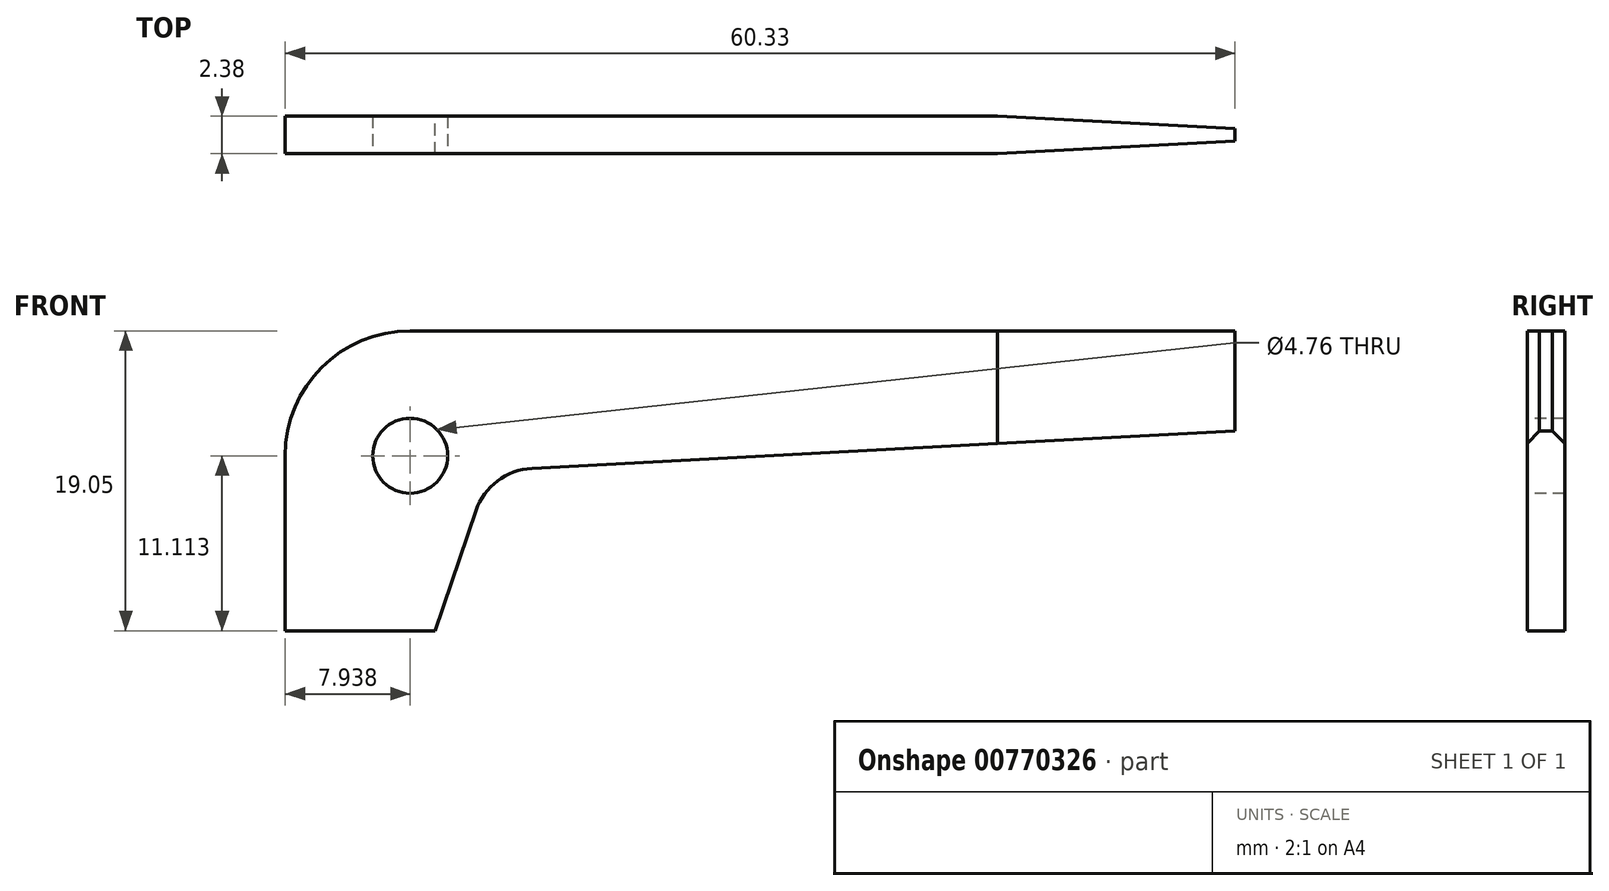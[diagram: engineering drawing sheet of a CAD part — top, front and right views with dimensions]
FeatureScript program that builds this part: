
annotation { "Feature Type Name" : "Feature", "Feature Type Description" : "" }
export const myFeature = defineFeature(function(context is Context, id is Id, definition is map)
    precondition{}
    {
        {
            var Q0;
            Q0=qCreatedBy(makeId("Front.planeOp"),FACE);
            var sketch = newSketch(context, id + "F0", { "sketchPlane" : qUnion([Q0])});
            skLineSegment(sketch, "E0.top", {"start": v(7.94, 19.05) * mm, "end": v(60.33, 19.05) * mm});
            skLineSegment(sketch, "E0.left", {"start": v(0, 0) * mm, "end": v(0, 11.11) * mm});
            skLineSegment(sketch, "E1", {"start": v(9.52, 0) * mm, "end": v(12.12, 7.63) * mm});
            skLineSegment(sketch, "E2", {"start": v(60.33, 12.7) * mm, "end": v(15.66, 10.31) * mm});
            skLineSegment(sketch, "E3", {"start": v(0, 0) * mm, "end": v(9.53, 0) * mm});
            skLineSegment(sketch, "E4", {"start": v(60.33, 19.05) * mm, "end": v(60.33, 12.7) * mm});
            skArc(sketch, "E5", {"start": v(15.66, 10.31) * mm, "mid": v(13.48, 9.51) * mm, "end": v(12.12, 7.63) * mm});
            skPoint(sketch, "E6.visualSharp", {"position": v(0, 19.05) * mm});
            skArc(sketch, "E6.filletArc", {"start": v(7.94, 19.05) * mm, "mid": v(2.32, 16.73) * mm, "end": v(0, 11.11) * mm});
            skSolve(sketch);
        }
        {
            var Q0;
            Q0 = qSketchRegion(id + "F0", true);
            extrude(context, id + "F1", {"entities" : qUnion([Q0]), "depth" : 2.38 * mm, "offsetDistance" : 25.4 * mm});
        }
        {
            var Q0;
            Q0=makeQuery(id+"F1.opExtrude","CAP_FACE",FACE,{"disambiguationData":[OSD([sQuery(id+"F0.wireOp",EDGE,"E0.top"),sQuery(id+"F0.wireOp",EDGE,"E0.left"),sQuery(id+"F0.wireOp",EDGE,"E1"),sQuery(id+"F0.wireOp",EDGE,"E2"),sQuery(id+"F0.wireOp",EDGE,"E3"),sQuery(id+"F0.wireOp",EDGE,"E4"),sQuery(id+"F0.wireOp",EDGE,"E5"),sQuery(id+"F0.wireOp",EDGE,"E6.filletArc")])],"isStart":false});
            var sketch = newSketch(context, id + "F2", { "sketchPlane" : qUnion([Q0])});
            skCircle(sketch, "E7", {"center": v(7.94, 11.11) * mm, "radius": 2.38 * mm});
            skSolve(sketch);
        }
        {
            var Q0;
            Q0=makeQuery(id+"F2.imprint","IMPRINT",FACE,{"disambiguationData":[TD([[makeQuery(id+"F2.imprint","IMPRINT",EDGE,{"derivedFrom":sQuery(id+"F2.wireOp",EDGE,"E7")}),1.0]])]});
            extrude(context, id + "F3", {"entities" : qUnion([Q0]), "operationType" : NewBodyOperationType.REMOVE, "oppositeDirection" : true, "depth" : 25.4 * mm, "offsetDistance" : 25.4 * mm});
        }
        {
            var Q0;
            Q0=makeQuery(id+"F1.opExtrude","SWEPT_FACE",FACE,{"disambiguationData":[OSD([sQuery(id+"F0.wireOp",EDGE,"E0.top")])]});
            var sketch = newSketch(context, id + "F4", { "sketchPlane" : qUnion([Q0])});
            skLineSegment(sketch, "E8", {"start": v(45.24, 0) * mm, "end": v(60.33, -0.8) * mm});
            skLineSegment(sketch, "E9", {"start": v(60.33, -0.8) * mm, "end": v(60.33, 0) * mm});
            skLineSegment(sketch, "E10", {"start": v(60.33, 0) * mm, "end": v(45.24, 0) * mm});
            skLineSegment(sketch, "E11", {"start": v(45.24, -2.38) * mm, "end": v(60.33, -1.6) * mm});
            skLineSegment(sketch, "E12", {"start": v(60.33, -1.6) * mm, "end": v(60.33, -2.38) * mm});
            skLineSegment(sketch, "E13", {"start": v(60.33, -2.38) * mm, "end": v(45.24, -2.38) * mm});
            skSolve(sketch);
        }
        {
            var Q0;
            Q0=makeQuery(id+"F4.imprint","IMPRINT",FACE,{"disambiguationData":[TD([[makeQuery(id+"F4.imprint","IMPRINT",EDGE,{"derivedFrom":sQuery(id+"F4.wireOp",EDGE,"E11")}),-1.0]])]});
            var Q1;
            Q1=makeQuery(id+"F4.imprint","IMPRINT",FACE,{"disambiguationData":[TD([[makeQuery(id+"F4.imprint","IMPRINT",EDGE,{"derivedFrom":sQuery(id+"F4.wireOp",EDGE,"E8")}),1.0]])]});
            extrude(context, id + "F5", {"entities" : qUnion([Q0, Q1]), "operationType" : NewBodyOperationType.REMOVE, "oppositeDirection" : true, "depth" : 25.4 * mm, "offsetDistance" : 25.4 * mm});
        }
    });
